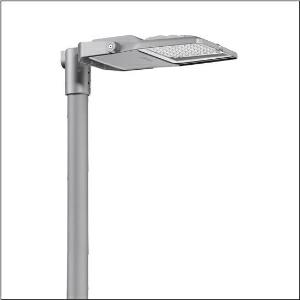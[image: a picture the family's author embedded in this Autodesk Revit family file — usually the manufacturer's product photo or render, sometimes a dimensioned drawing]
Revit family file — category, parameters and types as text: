
# Revit family: floodlight_fl_21_iq_mini___pl61_5xa7772b2c3a_0206
name_source: partatom
category: Lighting Fixtures
units: mm (PartAtom-declared; Revit-internal decimal feet)

## family parameters
Cut with Voids When Loaded = No
Host = Face
Light Source = No
Part Type = Normal
Room Calculation Point = No
Round Connector Dimension = Use Diameter
Shared = No

## types (1)
- --- (1 x LED, 6120 lm, 45.5 W, 3000K)
    Apparent Load = 46 VA
    CIE Flux Codes = 33 65 98 100 100
    Color Rendering = 70
    Color Temperature = 3000K
    Default Elevation = 1800 mm
    Description = Floodlight FL 21 iQ mini, floodlight, primary light control with lens, of PMMA, primary optical cover: protective disc, of toughened safety glass, transparent, light distribution: PL61, light emission: direct distribution, installation type: surface-mounted, LED, High Power LED, rated luminous flux: 6.120lm, luminous efficacy: 135lm/W, light colour: 730, colour temperature: 3000K, control: Auto-Match, Temp-Guard, Night-Set, Smart-Wire, Desk-Remote (wireless, voltage-free reading and setting of iQ features in the workshop via application-optimized NFC function/RFID function), optimised constant luminous flux control (CLO 2.0), Light-Fading, Lumen-Switch, with terminal, 6-pole, mains connection: 220..240V, AC, 50/60Hz, start of lifetime: 46W, end of service life: 48W, reduction: 22W, luminaire housing, of diecast aluminium, powder-coated, Siteco® metallic grey (DB 702S), corrosivity category C5 mid according to DIN EN ISO 12944, sealing non-destructively replaceable, please order mast flange separately, mast bracket, of steel, galvanised, powder-coated, protection rating (complete): IP66, insulation class (complete): insulation class II (safety insulation), certification: CE, ENEC, VDE, protection symbol: D, impact resistance: IK08, permissible operating ambient temperature: -40..+40°C, permissible operating ambient temperature for outdoor applications: -40..+50°C, standard: DIN EN 12944, LABS conformity tested according to VDMA 24364:2018-05, packaging unit: 1 piece

Light Distribution: PL61
    Height = 70 mm
    Lamp = 1 x LED
    Lamp Light Flux = 6120 lm
    Lamp Power = 45.5 W
    Lamp count = 1
    Length = 485 mm
    Luminous efficacy = 135 lm/W
    Manufacturer = Siteco
    ModVariant = No
    Model = 5XA7772B2C3A
    Number of Poles = 1
    OnlyDefault = Yes
    Power Factor = 1
    Product Name = Floodlight FL 21 iQ mini | PL61
    Product group = floodlight | pylon annexe
    ProductGroupID = 6200
    Protection Class = Protection class II
    Protection Degree = IP 66
    RLX_Detail_Level = 1
    RLX_Emergency_Light_Flux = 0 lm
    RLX_Emergency_Type = 0
    RLX_Emergency_Type_DB = No
    RlxData = <blob elided: 101221 chars, md5=df9abde6>
    Socket = socket
    Standby Power = 0 W
    System Light Flux = 6120 lm
    System Power = 46 W
    Type Comments = factory setting: luminous flux: 100 % | dim-lin: 254 | 463 mA
    Type Image = l_1007125.jpg
    URL = http://relux.com
    VarID = @adj_124511
    Voltage = 0 V
    Weight = 0.00 kg
    Width = 337 mm

## geometry (parser evidence)
native form markers: Blend x4, Sweep x12
no freeform markers — native parametric forms only
